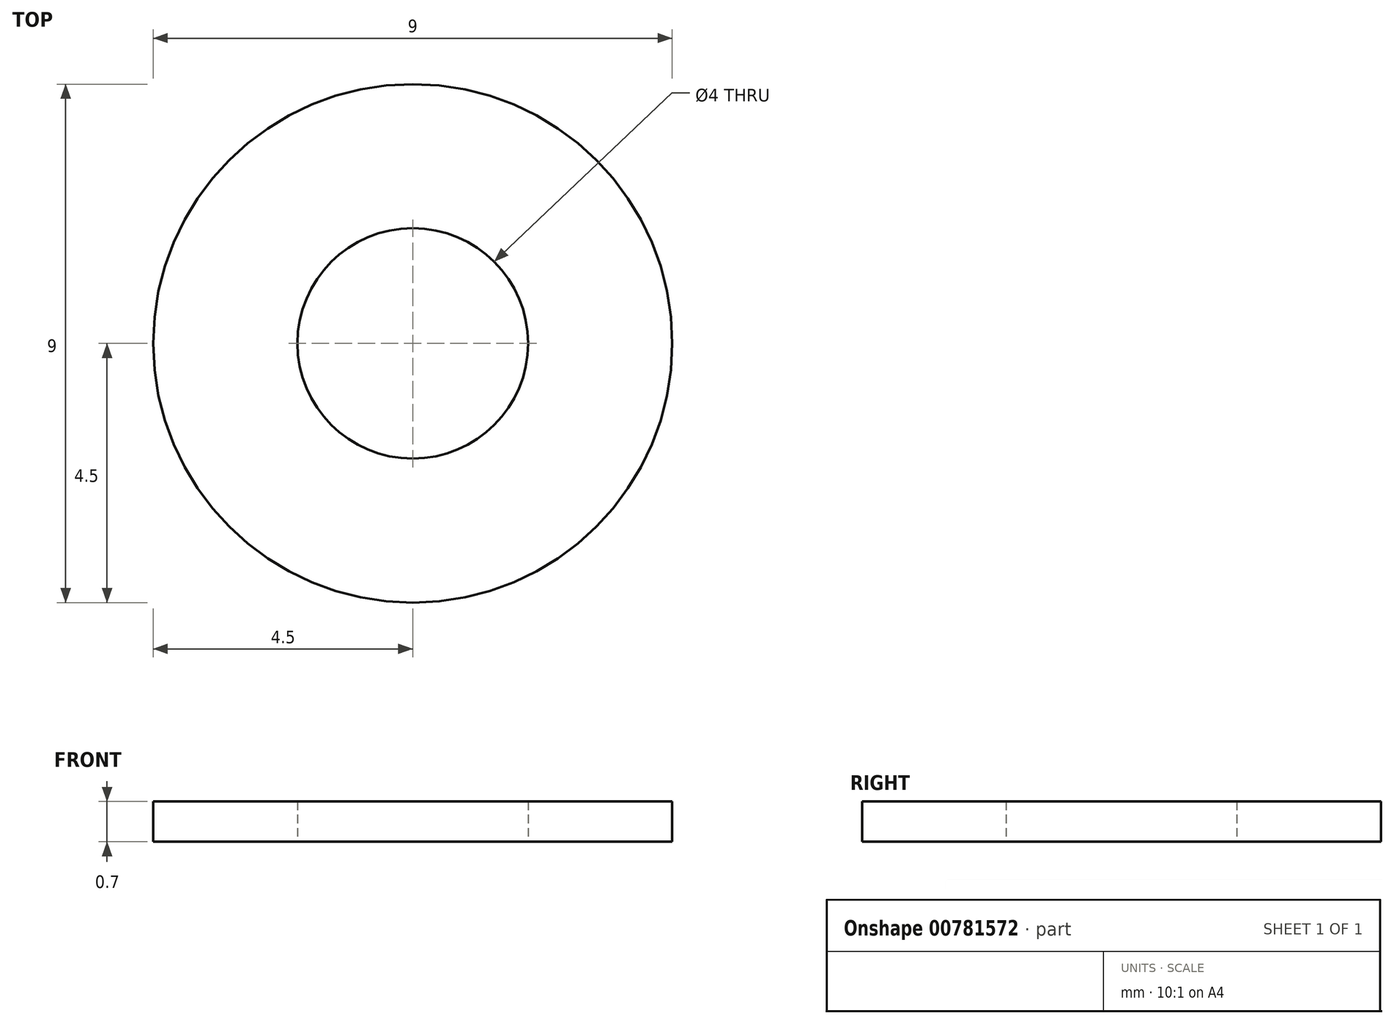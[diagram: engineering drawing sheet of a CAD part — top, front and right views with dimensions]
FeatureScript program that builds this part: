
annotation { "Feature Type Name" : "Feature", "Feature Type Description" : "" }
export const myFeature = defineFeature(function(context is Context, id is Id, definition is map)
    precondition{}
    {
        {
            var Q0;
            Q0=qCreatedBy(makeId("Top.planeOp"),FACE);
            var sketch = newSketch(context, id + "F0", { "sketchPlane" : qUnion([Q0])});
            skCircle(sketch, "E0", {"center": v(0, 0) * mm, "radius": 4.5 * mm});
            skCircle(sketch, "E1", {"center": v(0, 0) * mm, "radius": 2 * mm});
            skSolve(sketch);
        }
        {
            var Q0;
            Q0 = qSketchRegion(id + "F0", true);
            extrude(context, id + "F1", {"entities" : qUnion([Q0]), "endBound" : BoundingType.SYMMETRIC, "depth" : .7 * mm, "offsetDistance" : 25 * mm});
        }
    });
